# Revit family: Geberit Kombifix element za konzolnu WC šolju, 108 cm, sa ugradnim vodokotlićem Sigma 12 cm_PRO_101278
name_source: partatom
category: Plumbing Fixtures
units: mm (PartAtom-declared; Revit-internal decimal feet)

## family parameters
Always vertical = Yes
Cut with Voids When Loaded = No
OmniClass Number = 23.31.00.00
Part Type = Normal
Room Calculation Point = Yes
Round Connector Dimension = Use Diameter
Shared = No
Work Plane-Based = No

## types (1)
- 110.366.00.5 Geberit Kombifix element za konzolnu WC šolju, 108 cm, sa ugradnim vodokotlićem Sigma 12 cm
    B = 420 mm  [stored 1.37795 ft]
    BIM datoteka, datum izmene = 2024.01.26
    BIM datoteka, proizvođač = Geberit
    BIM datoteka, verzija = GEB MG 1.5
    Broj artikla = 110.366.00.5
    CW Connection = Yes
    Default Elevation = 0 mm  [stored 0 ft]
    Description = Geberit Kombifix element za konzolnu WC šolju, 108 cm, sa ugradnim vodokotlićem Sigma 12 cm
    EAN code basic data = 4025416857860
    EAN kôd = 4025416857860
    Fabrički podešena količina ispiranja = 6 i 3 l
    GEB_culture = sr-RS
    GEB_generic_description = concealed cistern support frame for toilet
    GEB_generic_manufacturer = generic
    GEB_imperial_engineering = No
    GEB_metric_engineering = Yes
    GEB_pimversion = 24.02.14
    GEB_processing_type = T
    GEB_reference = PRO_101278
    GEB_translations = {"ATT_10673":"EAN code basic data","GEB_connection_diameter1":"Prečnik priključka 1","GEB_connection_diameter2":"Prečnik priključka 2","application_range":"Oblast primene","applicationPurposes":"Namene","ATT_10773":"Protočni pritisak","ATT_10807":"Opseg podešavanje veće količine vode za ispiranje","ATT_10811":"Opseg podešavanja manje količine vode za ispiranje","ATT_10832":"Maksimalna temperatura vode","ATT_10866":"Fabrički podešena količina ispiranja","brandName":"Robna marka","characteristics":"Svojstva","connection_description1":"Opis priključka 1","connection_description2":"Opis priključka 2","connection_type_c01":"Vrsta priključka kod priključka 01","connection_type_c02":"Vrsta priključka kod priključka 02","content_creator":"BIM datoteka, proizvođač","content_date_changed":"BIM datoteka, datum izmene","content_version":"BIM datoteka, verzija","name":"Naziv","productBrand":"Robna marka proizvoda","scopeOfDelivery":"Obim isporuke","type":"Tip","angle":"ugao","GEB_cut_length_c02":"Maksimalno skraćenje kod priključka 02","sanitary socket":"Spojnica za prelaz","rod spacing 180mm":"Razmak kačenja 180 mm","rod spacing 230mm":"Razmak kačenja 230 mm","warning":"Upozorenje","fixed_material":"Osnovni materijal","fixed_material_01":"Osnovni materijal 01","fixed_material_02":"Osnovni materijal 02","fixed_material_03":"Osnovni materijal 03","fixed_material_04":"Osnovni materijal 04","ATT_10931":"B","ATT_10951":"H","ATT_380239":"T","key 1000":"Broj artikla","key 3000":"EAN kôd"}
    GEB_use_DN = Yes
    H = 1080 mm  [stored 3.54331 ft]
    H1 = 230 mm  [stored 0.754593 ft]
    H2 = 330 mm  [stored 1.08268 ft]
    HW Connection = No
    HWFU = 0
    IfcDescription = Geberit Kombifix element za konzolnu WC šolju, 108 cm, sa ugradnim vodokotlićem Sigma 12 cm
    IfcExportAs = IfcSanitaryTerminal
    IfcExportType = CISTERN
    LOD300 = No
    LOD400 = Yes
    Maksimalna temperatura vode = 25 °C
    Manufacturer = Geberit
    Model = Sigma 12 cm
    Namene = Za ozidane zidove
Za ugradnju u predzidne konstrukcije delimične ili visine etaže
Za konzolne WC šolje sa priključnim dimenzijama prema propisu EN 33:2011
Za jednokoličinsko, dvokoličinsko ili start/stop ispiranje
    Naziv = Geberit Kombifix element za konzolnu WC šolju, 108 cm, sa ugradnim vodokotlićem Sigma 12 cm
    Obim isporuke = Priključak vode R 1/2", kompatibilan sa MF adapterom, sa integrisanim ugaonim ventilom i ručnim točkićem
Građevinska zaštita za revizioni otvor
Priključni set za WC, ø 90 mm
Priključno koleno od PE-HD, ø 90 mm
Spojnica za prelaz od PE-HD, ø 90 / 110 mm
2 zaštitna čepa
Set zvučne izolacije
2 navojne šipke M12
Materijal za pričvršćivanje
    Oblast primene = sanitary systems
    Opis priključka 1 = cold water in
    Opis priključka 2 = sanitary out
    Opseg podešavanja manje količine vode za ispiranje = 2-4 l
    Opseg podešavanje veće količine vode za ispiranje = 4 / 4.5 / 6 / 7.5 l
    Osnovni materijal = Geberit, Plastic, Opaque white
    Osnovni materijal 01 = Geberit, Steel, Paint Finish, Blue
    Osnovni materijal 02 = Geberit, Laminate, Ivory, Matte
    Osnovni materijal 03 = Geberit, Steel, galvanized
    Osnovni materijal 04 = Geberit, PE-HD, Black
    Protočni pritisak = 0.1-10 bar
    Robna marka = Geberit
    Robna marka proizvoda = Kombifix
    Svojstva = Montažni ram, završna obrada pečenim lakom
Montažni ram sa četiri pričvrsna ugaonika
Dubina montaže, podesiva, 12–20,5 cm
Priključno koleno koje se može montirati bez alata
Učvršćivanje priključnog kolena za montažu bez alata sa prednje strane
Ugradni vodokotlić sa aktiviranjem sa prednje strane
Ugradni vodokotlić sa izolacijom protiv kondenzacije
Kod fabričkog podešavanja moguće je automatsko naknadno ispiranje
Radovi na montaži i servisu na ugradnom vodokotliću bez alata
Priključak za vodu, pozadi ili gore na sredini
Građevinska zaštita štiti otvor za servisiranje od vlage i prljavštine
Građevinska zaštita za revizioni otvor koja se može seći prema dužini
Sa praznom cevi za dovod vode ka priključku Geberit AquaClean WC sa tušem
Učvršćenje za priključak električnog napajanja
    T = 120 mm  [stored 0.393701 ft]
    Tip = Sigma 12 cm
    Vent Connection = No
    Waste Connection = Yes
    adapter_socket_included = Yes
    cistern_bottom = 450 mm  [stored 1.47638 ft]
    cistern_depth2 = 70 mm  [stored 0.229659 ft]
    cistern_front_offset = 2 mm  [stored 0.00656168 ft]
    cistern_width = 416 mm
    connection_bend_included = Yes
    cw_h = 35 mm  [stored 0.114829 ft]
    inlet_flow = 0.1 L/s
    outlet_flow = 0.0 L/s
    rod_width_180 = 180 mm  [stored 0.590551 ft]
    rod_width_230 = 230 mm  [stored 0.754593 ft]
    use_SoD_csv = Yes

note: [stored X ft] marks values corroborated as IEEE doubles in the binary element streams (Revit-internal decimal feet)

## geometry (parser evidence)
native form markers: Blend x2, Sweep x7
no freeform markers — native parametric forms only
